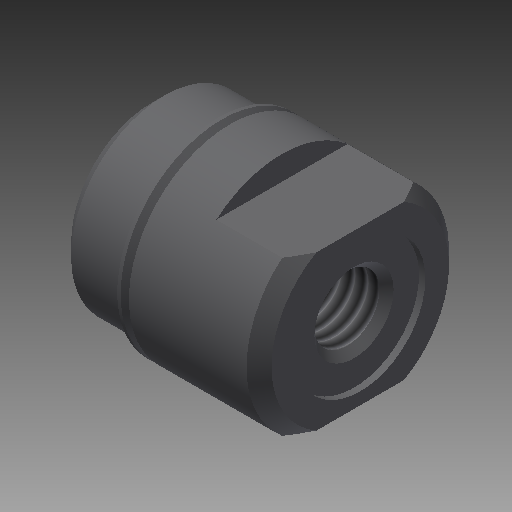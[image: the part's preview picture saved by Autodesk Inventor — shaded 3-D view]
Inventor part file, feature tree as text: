
AUTODESK INVENTOR PART (.ipt)
format: ipt  version: 2017 (Build 210142000, 142)  size: 243,712 bytes
history: native  units: in
note: dims shown in document units (in); Inventor stores cm internally (conversion verified against a paired STEP export)
features: other x112, sketch x5, revolve x2, hole x2, extrude x1
ambient origin geometry x8: Origin, YZ Plane, XZ Plane, XY Plane, X Axis, Y Axis, Z Axis, Center Point
bodies: Solid1 (feature_tree)
feature tree (122):
  revolve  "Revolution1"  [1 undecoded]
  hole  "Hole1"  [1 undecoded]
  hole  "Hole2"  [1 undecoded]
  extrude  "Extrusion1"  [1 undecoded]
  revolve  "Revolution2"  [1 undecoded]
  other  "cut1_XY"
  other  "cut1_YZ"
  other  "cut1_ZX"
  other  "cut1_X"
  other  "cut1_Y"
  other  "cut1_Z"
  other  "cut1_Center"
  other  "cut2_XY"
  other  "cut2_YZ"
  other  "cut2_ZX"
  other  "cut2_X"
  other  "cut2_Y"
  other  "cut2_Z"
  other  "cut2_Center"
  other  "cutf1_XY"
  other  "cutf1_YZ"
  other  "cutf1_ZX"
  other  "cutf1_X"
  other  "cutf1_Y"
  other  "cutf1_Z"
  other  "cutf1_Center"
  other  "cutf2_XY"
  other  "cutf2_YZ"
  other  "cutf2_ZX"
  other  "cutf2_X"
  other  "cutf2_Y"
  other  "cutf2_Z"
  other  "cutf2_Center"
  other  "lovra_XY"
  other  "lovra_YZ"
  other  "lovra_ZX"
  other  "lovra_X"
  other  "lovra_Y"
  other  "lovra_Z"
  other  "lovra_Center"
  other  "lovra1_XY"
  other  "lovra1_YZ"
  other  "lovra1_ZX"
  other  "lovra1_X"
  other  "lovra1_Y"
  other  "lovra1_Z"
  other  "lovra1_Center"
  other  "lovra2_XY"
  other  "lovra2_YZ"
  other  "lovra2_ZX"
  other  "lovra2_X"
  other  "lovra2_Y"
  other  "lovra2_Z"
  other  "lovra2_Center"
  other  "lovra21_XY"
  other  "lovra21_YZ"
  other  "lovra21_ZX"
  other  "lovra21_X"
  other  "lovra21_Y"
  other  "lovra21_Z"
  other  "lovra21_Center"
  other  "lovra22_XY"
  other  "lovra22_YZ"
  other  "lovra22_ZX"
  other  "lovra22_X"
  other  "lovra22_Y"
  other  "lovra22_Z"
  other  "lovra22_Center"
  other  "lovra3_XY"
  other  "lovra3_YZ"
  other  "lovra3_ZX"
  other  "lovra3_X"
  other  "lovra3_Y"
  other  "lovra3_Z"
  other  "lovra3_Center"
  other  "olen_XY"
  other  "olen_YZ"
  other  "olen_ZX"
  other  "olen_X"
  other  "olen_Y"
  other  "olen_Z"
  other  "olen_Center"
  other  "to_mounting_bracket_XY"
  other  "to_mounting_bracket_YZ"
  other  "to_mounting_bracket_ZX"
  other  "to_mounting_bracket_X"
  other  "to_mounting_bracket_Y"
  other  "to_mounting_bracket_Z"
  other  "to_mounting_bracket_Center"
  other  "to_nut_XY"
  other  "to_nut_YZ"
  other  "to_nut_ZX"
  other  "to_nut_X"
  other  "to_nut_Y"
  other  "to_nut_Z"
  other  "to_nut_Center"
  other  "to_pin_XY"
  other  "to_pin_YZ"
  other  "to_pin_ZX"
  other  "to_pin_X"
  other  "to_pin_Y"
  other  "to_pin_Z"
  other  "to_pin_Center"
  other  "to_screw_XY"
  other  "to_screw_YZ"
  other  "to_screw_ZX"
  other  "to_screw_X"
  other  "to_screw_Y"
  other  "to_screw_Z"
  other  "to_screw_Center"
  other  "to_tube_XY"
  other  "to_tube_YZ"
  other  "to_tube_ZX"
  other  "to_tube_X"
  other  "to_tube_Y"
  other  "to_tube_Z"
  other  "to_tube_Center"
  sketch  "Sketch_1"  dims[d0=360.0deg]
  sketch  "Sketch2"  dims[d1=0.312in d2=0.75in d3=0.375in d4=0.25in d5=0.5635in d6=0.015in d7=0.0in]
  sketch  "Sketch3"  dims[d8=0.156in d9=0.2169in d10=0.19in d11=0.25in d12=90.0deg d13=0.485in d14=0.0in d15=0.188in d16=0.0in]
  sketch  "Sketch_5"  dims[d17=360.0deg d18=0.0in d19=0.0in d20=0.0in d21=0.0in]
  sketch  "Sketch_24"
note: 5 required parameter values undecoded (feature->parameter linkage not recoverable at this tier; creation-order binding heuristic only, values carry confidence <= 0.55)